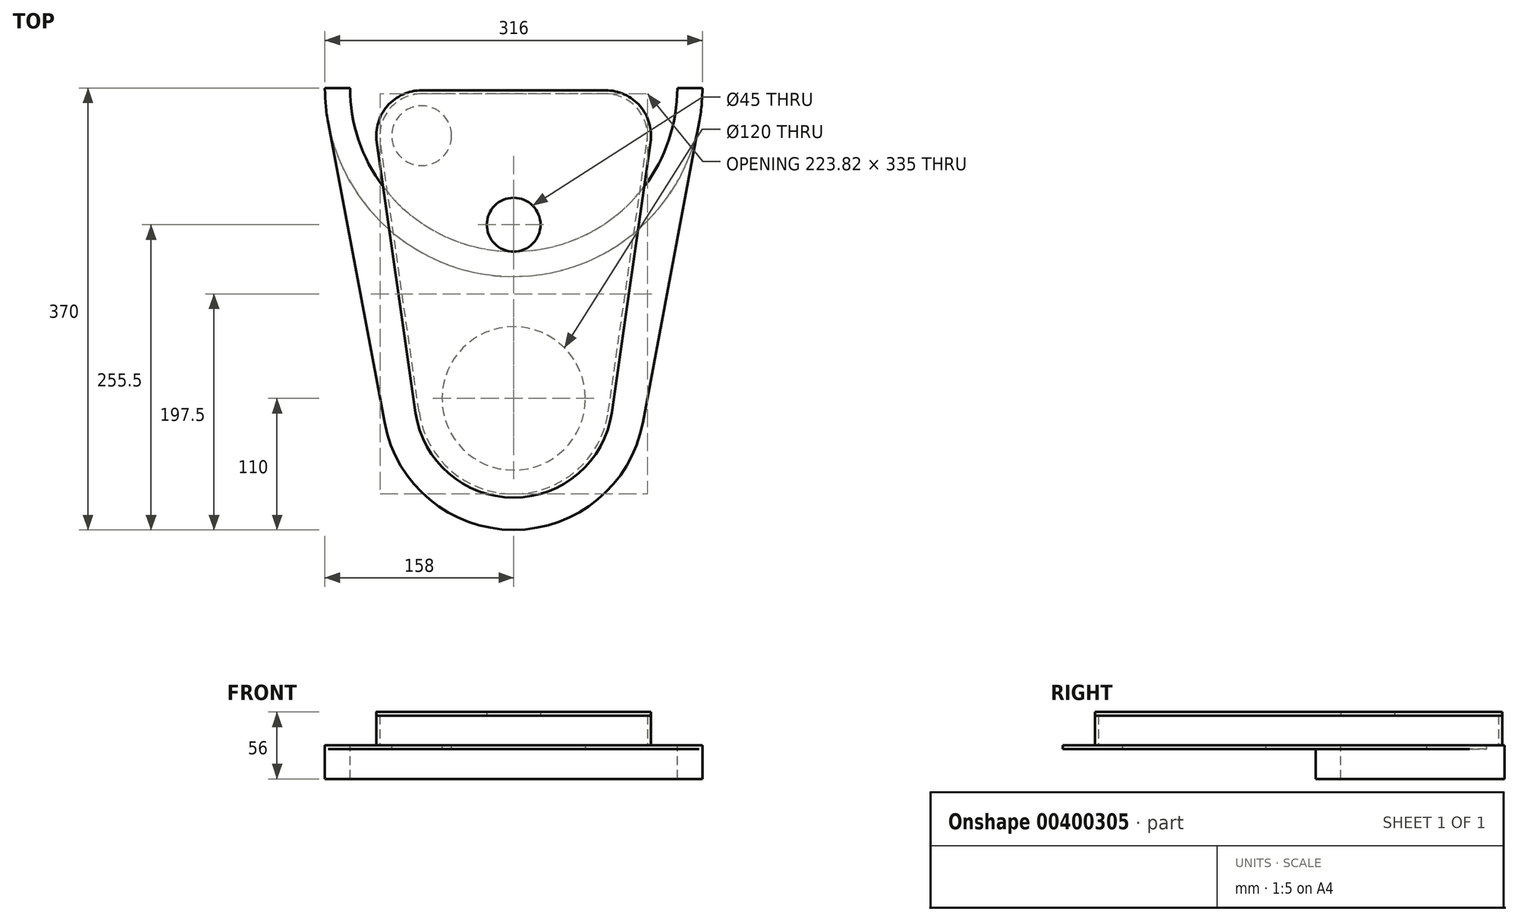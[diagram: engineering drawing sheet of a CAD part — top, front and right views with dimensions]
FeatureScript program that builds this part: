
annotation { "Feature Type Name" : "Feature", "Feature Type Description" : "" }
export const myFeature = defineFeature(function(context is Context, id is Id, definition is map)
    precondition{}
    {
        {
            var Q0;
            Q0=qCreatedBy(makeId("Top.planeOp"),FACE);
            var sketch = newSketch(context, id + "F0", { "sketchPlane" : qUnion([Q0])});
            skArc(sketch, "E0", {"start": v(-158, 0) * mm, "mid": v(0, -158) * mm, "end": v(158, 0) * mm});
            skLineSegment(sketch, "E1", {"start": v(-155.28, -29.17) * mm, "end": v(-108.1, -280.3) * mm});
            skLineSegment(sketch, "E2", {"start": v(155.28, -29.17) * mm, "end": v(108.1, -280.3) * mm});
            skArc(sketch, "E3", {"start": v(-108.1, -280.3) * mm, "mid": v(0, -370) * mm, "end": v(108.1, -280.3) * mm});
            skLineSegment(sketch, "E4", {"start": v(-158, 0) * mm, "end": v(158, 0) * mm});
            skCircle(sketch, "E5", {"center": v(0, -260) * mm, "radius": 60 * mm});
            skArc(sketch, "E6", {"start": v(-137, 0) * mm, "mid": v(0, -137) * mm, "end": v(137, 0) * mm});
            skSolve(sketch);
        }
        {
            var Q0;
            {var subQ0=sQuery(id+"F0.wireOp",EDGE,"E6");Q0=makeQuery(id+"F0.imprint","IMPRINT",FACE,{"disambiguationData":[TD([[makeQuery(id+"F0.imprint","IMPRINT",EDGE,{"derivedFrom":subQ0}),1.0]])]});}
            var Q1;
            {var subQ5=sQuery(id+"F0.wireOp",EDGE,"E6");Q1=makeQuery(id+"F0.imprint","IMPRINT",FACE,{"disambiguationData":[TD([[makeQuery(id+"F0.imprint","IMPRINT",EDGE,{"derivedFrom":subQ5}),-1.0]])]});}
            var Q2;
            {var subQ1=sQuery(id+"F0.wireOp",EDGE,"E1");Q2=makeQuery(id+"F0.imprint","IMPRINT",FACE,{"disambiguationData":[TD([[makeQuery(id+"F0.imprint","IMPRINT",EDGE,{"derivedFrom":subQ1}),1.0]])]});}
            extrude(context, id + "F1", {"entities" : qUnion([Q0, Q1, Q2]), "depth" : 3 * mm});
        }
        {
            var Q0;
            {var subQ5=sQuery(id+"F0.wireOp",EDGE,"E6");Q0=makeQuery(id+"F0.imprint","IMPRINT",FACE,{"disambiguationData":[TD([[makeQuery(id+"F0.imprint","IMPRINT",EDGE,{"derivedFrom":subQ5}),-1.0]])]});}
            extrude(context, id + "F2", {"entities" : qUnion([Q0]), "operationType" : NewBodyOperationType.ADD, "oppositeDirection" : true, "depth" : 25 * mm});
        }
        {
            var Q0;
            Q0=makeQuery(id+"F1.opExtrude","CAP_FACE",FACE,{"disambiguationData":[OSD([sQuery(id+"F0.wireOp",EDGE,"E0"),sQuery(id+"F0.wireOp",EDGE,"E1"),sQuery(id+"F0.wireOp",EDGE,"E2"),sQuery(id+"F0.wireOp",EDGE,"E3"),sQuery(id+"F0.wireOp",EDGE,"E4"),sQuery(id+"F0.wireOp",EDGE,"E5")])],"isStart":false});
            var sketch = newSketch(context, id + "F3", { "sketchPlane" : qUnion([Q0])});
            skPoint(sketch, "E7.middle", {"position": v(0, -128.11) * mm});
            skLineSegment(sketch, "E8", {"start": v(0, 0) * mm, "end": v(0, -262.67) * mm, "construction": true});
            skArc(sketch, "E9.0", {"start": v(-137, 0) * mm, "mid": v(0, -137) * mm, "end": v(137, 0) * mm});
            skCircle(sketch, "E10", {"center": v(77, -40) * mm, "radius": 25 * mm});
            skCircle(sketch, "E11.MirrorC", {"center": v(-77, -40) * mm, "radius": 25 * mm});
            skCircle(sketch, "E12", {"center": v(0, -87) * mm, "radius": 50 * mm});
            skSolve(sketch);
        }
        {
            var Q0;
            Q0=makeQuery(id+"F3.imprint","IMPRINT",FACE,{"disambiguationData":[TD([[makeQuery(id+"F3.imprint","IMPRINT",EDGE,{"derivedFrom":sQuery(id+"F3.wireOp",EDGE,"E7.bottom")}),-1.0]])]});
            var Q1;
            Q1=makeQuery(id+"F3.imprint","IMPRINT",FACE,{"disambiguationData":[TD([[makeQuery(id+"F3.imprint","IMPRINT",EDGE,{"derivedFrom":sQuery(id+"F3.wireOp",EDGE,"AjtL0WRP-HgkU-muXz-9kWA-N0n2J3sxUqPO.bottom")}),1.0]])]});
            var Q2;
            Q2=makeQuery(id+"F3.imprint","IMPRINT",FACE,{"disambiguationData":[TD([[makeQuery(id+"F3.imprint","IMPRINT",EDGE,{"derivedFrom":sQuery(id+"F3.wireOp",EDGE,"hbn4nmRc-nMSa-E17o-YtSg-FN6U9JiJ0E1N")}),1.0]])]});
            var Q3;
            Q3=makeQuery(id+"F3.imprint","IMPRINT",FACE,{"disambiguationData":[TD([[makeQuery(id+"F3.imprint","IMPRINT",EDGE,{"derivedFrom":sQuery(id+"F3.wireOp",EDGE,"19e78cce-7d75-47f0-a43c-a74716353a520.MirrorC")}),-1.0]])]});
            var Q4;
            Q4=makeQuery(id+"F3.imprint","IMPRINT",FACE,{"disambiguationData":[TD([[makeQuery(id+"F3.imprint","IMPRINT",EDGE,{"derivedFrom":sQuery(id+"F3.wireOp",EDGE,"rSp8Xc3M-vjKt-TzCo-SzVD-CnCDpnyHxxwz")}),1.0]])]});
            var Q5;
            Q5=makeQuery(id+"F3.imprint","IMPRINT",FACE,{"disambiguationData":[TD([[makeQuery(id+"F3.imprint","IMPRINT",EDGE,{"derivedFrom":sQuery(id+"F3.wireOp",EDGE,"ANmGfits-o05E-JOYX-5jTR-aISLuBRczIhw.bottom")}),-1.0]])]});
            var Q6;
            Q6=makeQuery(id+"F3.imprint","IMPRINT",FACE,{"disambiguationData":[TD([[makeQuery(id+"F3.imprint","IMPRINT",EDGE,{"derivedFrom":sQuery(id+"F3.wireOp",EDGE,"E11.MirrorC")}),-1.0]])]});
            var Q7;
            Q7=makeQuery(id+"F3.imprint","IMPRINT",FACE,{"disambiguationData":[TD([[makeQuery(id+"F3.imprint","IMPRINT",EDGE,{"derivedFrom":sQuery(id+"F3.wireOp",EDGE,"E12")}),1.0]])]});
            var Q8;
            Q8=makeQuery(id+"F3.imprint","IMPRINT",FACE,{"disambiguationData":[TD([[makeQuery(id+"F3.imprint","IMPRINT",EDGE,{"derivedFrom":sQuery(id+"F3.wireOp",EDGE,"E10")}),1.0]])]});
            extrude(context, id + "F4", {"entities" : qUnion([Q0, Q1, Q2, Q3, Q4, Q5, Q6, Q7, Q8]), "operationType" : NewBodyOperationType.REMOVE, "endBound" : BoundingType.THROUGH_ALL, "oppositeDirection" : true, "depth" : 25 * mm});
        }
        {
            var Q0;
            Q0=makeQuery(id+"F1.opExtrude","CAP_FACE",FACE,{"disambiguationData":[OSD([sQuery(id+"F0.wireOp",EDGE,"E0"),sQuery(id+"F0.wireOp",EDGE,"E1"),sQuery(id+"F0.wireOp",EDGE,"E2"),sQuery(id+"F0.wireOp",EDGE,"E3"),sQuery(id+"F0.wireOp",EDGE,"E4"),sQuery(id+"F0.wireOp",EDGE,"E5")])],"isStart":false});
            var sketch = newSketch(context, id + "F5", { "sketchPlane" : qUnion([Q0])});
            skArc(sketch, "E13.1", {"start": v(-79.2, -271.35) * mm, "mid": v(0, -340) * mm, "end": v(79.2, -271.35) * mm});
            skArc(sketch, "E14", {"start": v(-77, -5) * mm, "mid": v(-103.45, -17.07) * mm, "end": v(-111.65, -44.97) * mm});
            skArc(sketch, "E15", {"start": v(111.65, -44.97) * mm, "mid": v(103.45, -17.07) * mm, "end": v(77, -5) * mm});
            skLineSegment(sketch, "E16", {"start": v(-79.2, -271.35) * mm, "end": v(-111.65, -44.97) * mm});
            skLineSegment(sketch, "E17", {"start": v(79.2, -271.35) * mm, "end": v(111.65, -44.97) * mm});
            skLineSegment(sketch, "E18", {"start": v(77, -5) * mm, "end": v(-77, -5) * mm});
            skArc(sketch, "E19.0", {"start": v(-82.16, -271.78) * mm, "mid": v(0, -343) * mm, "end": v(82.16, -271.78) * mm});
            skArc(sketch, "E19.1", {"start": v(-77, -2) * mm, "mid": v(-105.71, -15.1) * mm, "end": v(-114.62, -45.4) * mm});
            skLineSegment(sketch, "E19.2", {"start": v(77, -2) * mm, "end": v(-77, -2) * mm});
            skLineSegment(sketch, "E19.3", {"start": v(-82.16, -271.78) * mm, "end": v(-114.62, -45.4) * mm});
            skArc(sketch, "E19.4", {"start": v(114.62, -45.4) * mm, "mid": v(105.71, -15.1) * mm, "end": v(77, -2) * mm});
            skLineSegment(sketch, "E19.5", {"start": v(82.16, -271.78) * mm, "end": v(114.62, -45.4) * mm});
            skSolve(sketch);
        }
        {
            var Q0;
            Q0=makeQuery(id+"F5.imprint","IMPRINT",FACE,{"disambiguationData":[TD([[makeQuery(id+"F5.imprint","IMPRINT",EDGE,{"derivedFrom":sQuery(id+"F5.wireOp",EDGE,"qgkaUuCK-zfni-Eonx-vNHk-OwVKBBZdX0VA")}),-1.0]])]});
            var Q1;
            Q1=makeQuery(id+"F5.imprint","IMPRINT",FACE,{"disambiguationData":[TD([[makeQuery(id+"F5.imprint","IMPRINT",EDGE,{"derivedFrom":sQuery(id+"F5.wireOp",EDGE,"E13.1")}),-1.0]])]});
            extrude(context, id + "F6", {"entities" : qUnion([Q0, Q1]), "depth" : 25 * mm});
        }
        {
            var Q0;
            Q0=makeQuery(id+"F6.opExtrude","CAP_FACE",FACE,{"disambiguationData":[OSD([sQuery(id+"F5.wireOp",EDGE,"E13.1"),sQuery(id+"F5.wireOp",EDGE,"E14"),sQuery(id+"F5.wireOp",EDGE,"E15"),sQuery(id+"F5.wireOp",EDGE,"E16"),sQuery(id+"F5.wireOp",EDGE,"E17"),sQuery(id+"F5.wireOp",EDGE,"E18"),sQuery(id+"F5.wireOp",EDGE,"E19.0"),sQuery(id+"F5.wireOp",EDGE,"E19.1"),sQuery(id+"F5.wireOp",EDGE,"E19.2"),sQuery(id+"F5.wireOp",EDGE,"E19.3"),sQuery(id+"F5.wireOp",EDGE,"E19.4"),sQuery(id+"F5.wireOp",EDGE,"E19.5")])],"isStart":false});
            var sketch = newSketch(context, id + "F7", { "sketchPlane" : qUnion([Q0])});
            skLineSegment(sketch, "E20.0.0", {"start": v(82.16, -271.78) * mm, "end": v(114.62, -45.4) * mm});
            skArc(sketch, "E20.0.1", {"start": v(114.62, -45.4) * mm, "mid": v(105.71, -15.1) * mm, "end": v(77, -2) * mm});
            skLineSegment(sketch, "E20.0.2", {"start": v(77, -2) * mm, "end": v(-77, -2) * mm});
            skArc(sketch, "E20.0.3", {"start": v(-77, -2) * mm, "mid": v(-105.71, -15.1) * mm, "end": v(-114.62, -45.4) * mm});
            skLineSegment(sketch, "E20.0.4", {"start": v(-114.62, -45.4) * mm, "end": v(-82.16, -271.78) * mm});
            skArc(sketch, "E20.0.5", {"start": v(-82.16, -271.78) * mm, "mid": v(0, -343) * mm, "end": v(82.16, -271.78) * mm});
            skCircle(sketch, "E21", {"center": v(0, -114.5) * mm, "radius": 22.5 * mm});
            skCircle(sketch, "E22.0", {"center": v(0, -87) * mm, "radius": 50 * mm});
            skSolve(sketch);
        }
        {
            var Q0;
            Q0=makeQuery(id+"F7.imprint","IMPRINT",FACE,{"disambiguationData":[TD([[makeQuery(id+"F7.imprint","IMPRINT",EDGE,{"derivedFrom":sQuery(id+"F7.wireOp",EDGE,"6be0f923-56ff-4470-a68a-a1ff9abf1a37.0")}),-1.0]])]});
            var Q1;
            Q1=makeQuery(id+"F7.imprint","IMPRINT",FACE,{"disambiguationData":[TD([[makeQuery(id+"F7.imprint","IMPRINT",EDGE,{"derivedFrom":sQuery(id+"F7.wireOp",EDGE,"E20.0.0")}),1.0]])]});
            var Q2;
            Q2=makeQuery(id+"F7.imprint","IMPRINT",FACE,{"disambiguationData":[TD([[makeQuery(id+"F7.imprint","IMPRINT",EDGE,{"derivedFrom":makeQuery(id+"F6.opExtrude","CAP_EDGE",EDGE,{"disambiguationData":[OSD([sQuery(id+"F5.wireOp",EDGE,"E13.1")])],"isStart":false})}),1.0]])]});
            var Q3;
            {var subQ0=sQuery(id+"F7.wireOp",EDGE,"E21");Q3=makeQuery(id+"F7.imprint","IMPRINT",FACE,{"disambiguationData":[TD([[makeQuery(id+"F7.imprint","IMPRINT",EDGE,{"derivedFrom":subQ0}),-1.0]])]});}
            extrude(context, id + "F8", {"entities" : qUnion([Q0, Q1, Q2, Q3]), "depth" : 3 * mm});
        }
    });
